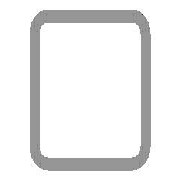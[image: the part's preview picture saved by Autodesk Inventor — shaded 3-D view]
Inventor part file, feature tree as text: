
AUTODESK INVENTOR PART (.ipt)
format: ipt  version: 2016 (Build 200138000, 138)  size: 139,264 bytes
history: native  units: mm (DEFAULTED — no unit token found)
features: other x4, sketch x3, plane x2, split x1
ambient origin geometry x8: Origin, YZ Plane, XZ Plane, XY Plane, X Axis, Y Axis, Z Axis, Center Point
bodies: Solid1 (feature_tree), Body (feature_tree)
feature tree (10):
  parser-record x1  (decoder bookkeeping rows leaked as tree rows — omitted from the tree; the rows remain in map.json)
  other  "Driven Length"
  other  "Start plane"
  other  "End plane"
  plane  "Work Plane4"
  split  "Split1"
  sketch  "Sketch"  dims[d7=4.0mm d9=25.0mm d11=25.0mm d12=2.0mm d13=-0.0mm d14=479.787868mm d15=12.5mm d16=12.5mm d17=90.0deg d18=479.787868mm]
  sketch  "Sketch3"  dims[d3=479.787868mm]
  plane  "Work Plane3"
  sketch  "Sketch4"  dims[d4=0.0mm]
